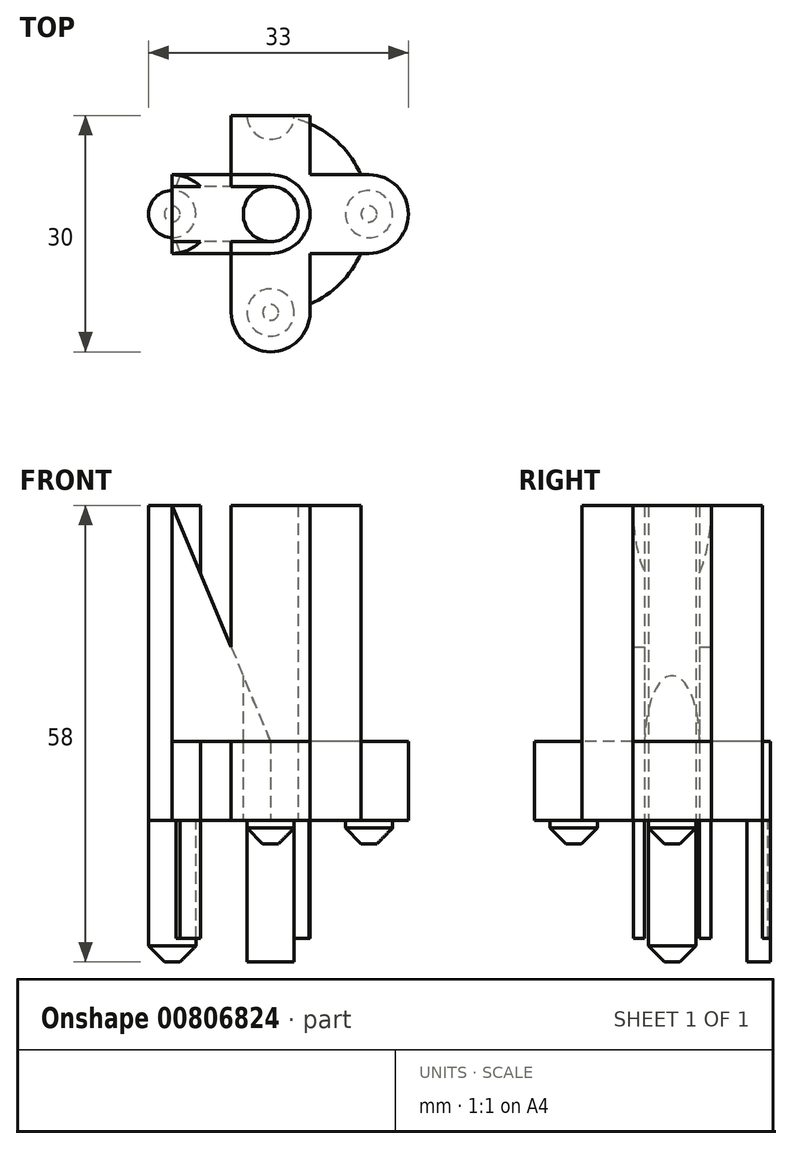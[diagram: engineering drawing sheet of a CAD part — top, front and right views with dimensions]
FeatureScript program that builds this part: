
annotation { "Feature Type Name" : "Feature", "Feature Type Description" : "" }
export const myFeature = defineFeature(function(context is Context, id is Id, definition is map)
    precondition{}
    {
        {
            var Q0;
            Q0=qCreatedBy(makeId("Top.planeOp"),FACE);
            var sketch = newSketch(context, id + "F0", { "sketchPlane" : qUnion([Q0])});
            skCircle(sketch, "E0", {"center": v(0, 0) * mm, "radius": 12.5 * mm});
            skCircle(sketch, "E1", {"center": v(0, 0) * mm, "radius": 3.5 * mm});
            skCircle(sketch, "E2", {"center": v(0, -12.5) * mm, "radius": 5 * mm});
            skCircle(sketch, "E3", {"center": v(0, 12.5) * mm, "radius": 5 * mm});
            skCircle(sketch, "E4", {"center": v(12.5, 0) * mm, "radius": 5 * mm});
            skCircle(sketch, "E5", {"center": v(-12.5, 0) * mm, "radius": 5 * mm});
            skCircle(sketch, "E6", {"center": v(-12.5, 0) * mm, "radius": 3 * mm});
            skCircle(sketch, "E7", {"center": v(0, 12.5) * mm, "radius": 3 * mm});
            skCircle(sketch, "E8", {"center": v(12.5, 0) * mm, "radius": 3 * mm});
            skCircle(sketch, "E9", {"center": v(0, -12.5) * mm, "radius": 3 * mm});
            skCircle(sketch, "E10", {"center": v(0, 0) * mm, "radius": 5 * mm});
            skLineSegment(sketch, "E11.bottom", {"start": v(0, 3.5) * mm, "end": v(-12.5, 3.5) * mm});
            skLineSegment(sketch, "E11.top", {"start": v(0, 5) * mm, "end": v(-12.5, 5) * mm});
            skLineSegment(sketch, "E11.left", {"start": v(0, 3.5) * mm, "end": v(0, 5) * mm});
            skLineSegment(sketch, "E11.right", {"start": v(-12.5, 3.5) * mm, "end": v(-12.5, 5) * mm});
            skLineSegment(sketch, "E12.bottom", {"start": v(0, -3.5) * mm, "end": v(-12.5, -3.5) * mm});
            skLineSegment(sketch, "E12.top", {"start": v(0, -5) * mm, "end": v(-12.5, -5) * mm});
            skLineSegment(sketch, "E12.left", {"start": v(0, -3.5) * mm, "end": v(0, -5) * mm});
            skLineSegment(sketch, "E12.right", {"start": v(-12.5, -3.5) * mm, "end": v(-12.5, -5) * mm});
            skLineSegment(sketch, "E13.bottom", {"start": v(5, 12.5) * mm, "end": v(-5, 12.5) * mm});
            skLineSegment(sketch, "E13.top", {"start": v(5, -12.5) * mm, "end": v(-5, -12.5) * mm});
            skLineSegment(sketch, "E13.left", {"start": v(5, 12.5) * mm, "end": v(5, -12.5) * mm});
            skLineSegment(sketch, "E13.right", {"start": v(-5, 12.5) * mm, "end": v(-5, -12.5) * mm});
            skLineSegment(sketch, "E14.bottom", {"start": v(12.5, 5) * mm, "end": v(-12.5, 5) * mm});
            skLineSegment(sketch, "E14.top", {"start": v(12.5, -5) * mm, "end": v(-12.5, -5) * mm});
            skLineSegment(sketch, "E14.left", {"start": v(12.5, 5) * mm, "end": v(12.5, -5) * mm});
            skLineSegment(sketch, "E14.right", {"start": v(-12.5, 5) * mm, "end": v(-12.5, -5) * mm});
            skSolve(sketch);
        }
        {
            var Q0;
            Q0=qCreatedBy(makeId("Front.planeOp"),FACE);
            var sketch = newSketch(context, id + "F1", { "sketchPlane" : qUnion([Q0])});
            skLineSegment(sketch, "E15", {"start": v(0, 0) * mm, "end": v(0, 10) * mm});
            skLineSegment(sketch, "E16", {"start": v(0, 10) * mm, "end": v(-12.5, 10) * mm});
            skLineSegment(sketch, "E17", {"start": v(-12.5, 10) * mm, "end": v(-12.5, 40) * mm});
            skLineSegment(sketch, "E18", {"start": v(-12.5, 40) * mm, "end": v(0, 10) * mm});
            skSolve(sketch);
        }
        {
            var Q0;
            Q0=makeQuery(id+"F1.imprint","IMPRINT",FACE,{"disambiguationData":[TD([[makeQuery(id+"F1.imprint","IMPRINT",EDGE,{"derivedFrom":sQuery(id+"F1.wireOp",EDGE,"E16")}),-1.0]])]});
            extrude(context, id + "F2", {"entities" : qUnion([Q0]), "endBound" : BoundingType.SYMMETRIC, "depth" : 10 * mm, "offsetDistance" : 25 * mm});
        }
        {
            var Q0;
            {var subQ0=sQuery(id+"F0.wireOp",EDGE,"E11.left");Q0=makeQuery(id+"F0.imprint","IMPRINT",FACE,{"disambiguationData":[TD([[makeQuery(id+"F0.imprint","IMPRINT",EDGE,{"derivedFrom":subQ0}),-1.0]])]});}
            var Q1;
            {var subQ0=sQuery(id+"F0.wireOp",EDGE,"E11.left");Q1=makeQuery(id+"F0.imprint","IMPRINT",FACE,{"disambiguationData":[TD([[makeQuery(id+"F0.imprint","IMPRINT",EDGE,{"derivedFrom":subQ0}),1.0]])]});}
            var Q2;
            {var subQ1=sQuery(id+"F0.wireOp",EDGE,"E10");var subQ3=sQuery(id+"F0.wireOp",EDGE,"E11.bottom");var subQ4=makeQuery(id+"F0.imprint","INTERSECT",VERTEX,{"derivedFrom":[subQ1,subQ3]});Q2=makeQuery(id+"F0.imprint","IMPRINT",FACE,{"disambiguationData":[TD([[makeQuery(id+"F0.imprint","IMPRINT",EDGE,{"disambiguationData":[TD([[subQ4,-1.0]])],"derivedFrom":subQ3}),-1.0]])]});}
            var Q3;
            {var subQ3=sQuery(id+"F0.wireOp",EDGE,"E14.bottom");var subQ7=sQuery(id+"F0.wireOp",EDGE,"E0");var subQ9=makeQuery(id+"F0.imprint","INTERSECT",VERTEX,{"disambiguationData":[OD(1.0)],"derivedFrom":[subQ7,subQ3]});Q3=makeQuery(id+"F0.imprint","IMPRINT",FACE,{"disambiguationData":[TD([[makeQuery(id+"F0.imprint","IMPRINT",EDGE,{"disambiguationData":[TD([[subQ9,-1.0]])],"derivedFrom":subQ7}),1.0]])]});}
            var Q4;
            {var subQ0=sQuery(id+"F0.wireOp",EDGE,"E5");var subQ1=sQuery(id+"F0.wireOp",EDGE,"E0");var subQ2=makeQuery(id+"F0.imprint","INTERSECT",VERTEX,{"disambiguationData":[OD(0.0)],"derivedFrom":[subQ1,subQ0]});Q4=makeQuery(id+"F0.imprint","IMPRINT",FACE,{"disambiguationData":[TD([[makeQuery(id+"F0.imprint","IMPRINT",EDGE,{"disambiguationData":[TD([[subQ2,-1.0]])],"derivedFrom":subQ1}),1.0]])]});}
            var Q5;
            {var subQ0=sQuery(id+"F0.wireOp",EDGE,"E5");var subQ1=sQuery(id+"F0.wireOp",EDGE,"E0");var subQ2=makeQuery(id+"F0.imprint","INTERSECT",VERTEX,{"disambiguationData":[OD(0.0)],"derivedFrom":[subQ1,subQ0]});Q5=makeQuery(id+"F0.imprint","IMPRINT",FACE,{"disambiguationData":[TD([[makeQuery(id+"F0.imprint","IMPRINT",EDGE,{"disambiguationData":[TD([[subQ2,-1.0]])],"derivedFrom":subQ1}),-1.0]])]});}
            var Q6;
            {var subQ0=sQuery(id+"F0.wireOp",EDGE,"E12.bottom");var subQ1=sQuery(id+"F0.wireOp",EDGE,"E0");var subQ2=makeQuery(id+"F0.imprint","INTERSECT",VERTEX,{"derivedFrom":[subQ1,subQ0]});Q6=makeQuery(id+"F0.imprint","IMPRINT",FACE,{"disambiguationData":[TD([[makeQuery(id+"F0.imprint","IMPRINT",EDGE,{"disambiguationData":[TD([[subQ2,-1.0]])],"derivedFrom":subQ1}),-1.0]])]});}
            var Q7;
            {var subQ0=sQuery(id+"F0.wireOp",EDGE,"E12.bottom");var subQ1=sQuery(id+"F0.wireOp",EDGE,"E0");var subQ2=makeQuery(id+"F0.imprint","INTERSECT",VERTEX,{"derivedFrom":[subQ1,subQ0]});Q7=makeQuery(id+"F0.imprint","IMPRINT",FACE,{"disambiguationData":[TD([[makeQuery(id+"F0.imprint","IMPRINT",EDGE,{"disambiguationData":[TD([[subQ2,-1.0]])],"derivedFrom":subQ1}),1.0]])]});}
            var Q8;
            {var subQ5=sQuery(id+"F0.wireOp",EDGE,"E14.top");var subQ7=sQuery(id+"F0.wireOp",EDGE,"E0");var subQ9=makeQuery(id+"F0.imprint","INTERSECT",VERTEX,{"disambiguationData":[OD(0.0)],"derivedFrom":[subQ7,subQ5]});Q8=makeQuery(id+"F0.imprint","IMPRINT",FACE,{"disambiguationData":[TD([[makeQuery(id+"F0.imprint","IMPRINT",EDGE,{"disambiguationData":[TD([[subQ9,1.0]])],"derivedFrom":subQ7}),1.0]])]});}
            var Q9;
            {var subQ1=sQuery(id+"F0.wireOp",EDGE,"E10");var subQ3=sQuery(id+"F0.wireOp",EDGE,"E12.bottom");var subQ4=makeQuery(id+"F0.imprint","INTERSECT",VERTEX,{"derivedFrom":[subQ1,subQ3]});Q9=makeQuery(id+"F0.imprint","IMPRINT",FACE,{"disambiguationData":[TD([[makeQuery(id+"F0.imprint","IMPRINT",EDGE,{"disambiguationData":[TD([[subQ4,-1.0]])],"derivedFrom":subQ3}),1.0]])]});}
            var Q10;
            {var subQ0=sQuery(id+"F0.wireOp",EDGE,"E12.left");Q10=makeQuery(id+"F0.imprint","IMPRINT",FACE,{"disambiguationData":[TD([[makeQuery(id+"F0.imprint","IMPRINT",EDGE,{"derivedFrom":subQ0}),-1.0]])]});}
            var Q11;
            {var subQ0=sQuery(id+"F0.wireOp",EDGE,"E14.top");var subQ1=sQuery(id+"F0.wireOp",EDGE,"E0");var subQ2=makeQuery(id+"F0.imprint","INTERSECT",VERTEX,{"disambiguationData":[OD(0.0)],"derivedFrom":[subQ1,subQ0]});Q11=makeQuery(id+"F0.imprint","IMPRINT",FACE,{"disambiguationData":[TD([[makeQuery(id+"F0.imprint","IMPRINT",EDGE,{"disambiguationData":[TD([[subQ2,1.0]])],"derivedFrom":subQ1}),-1.0]])]});}
            var Q12;
            {var subQ0=sQuery(id+"F0.wireOp",EDGE,"E14.bottom");var subQ1=sQuery(id+"F0.wireOp",EDGE,"E0");var subQ2=makeQuery(id+"F0.imprint","INTERSECT",VERTEX,{"disambiguationData":[OD(1.0)],"derivedFrom":[subQ1,subQ0]});Q12=makeQuery(id+"F0.imprint","IMPRINT",FACE,{"disambiguationData":[TD([[makeQuery(id+"F0.imprint","IMPRINT",EDGE,{"disambiguationData":[TD([[subQ2,-1.0]])],"derivedFrom":subQ1}),-1.0]])]});}
            var Q13;
            {var subQ0=sQuery(id+"F0.wireOp",EDGE,"E14.right");var subQ4=makeQuery(id+"F0.imprint","INTERSECT",VERTEX,{"derivedFrom":[sQuery(id+"F0.wireOp",EDGE,"E0"),subQ0]});Q13=makeQuery(id+"F0.imprint","IMPRINT",FACE,{"disambiguationData":[TD([[makeQuery(id+"F0.imprint","IMPRINT",EDGE,{"disambiguationData":[TD([[subQ4,1.0]])],"derivedFrom":subQ0}),-1.0]])]});}
            var Q14;
            {var subQ0=sQuery(id+"F0.wireOp",EDGE,"E14.right");var subQ1=sQuery(id+"F0.wireOp",EDGE,"E5");var subQ2=makeQuery(id+"F0.imprint","INTERSECT",VERTEX,{"derivedFrom":[subQ1,sQuery(id+"F0.wireOp",EDGE,"E14.bottom"),subQ0]});Q14=makeQuery(id+"F0.imprint","IMPRINT",FACE,{"disambiguationData":[TD([[makeQuery(id+"F0.imprint","IMPRINT",EDGE,{"disambiguationData":[TD([[subQ2,-1.0]])],"derivedFrom":subQ1}),1.0]])]});}
            extrude(context, id + "F3", {"entities" : qUnion([Q0, Q1, Q2, Q3, Q4, Q5, Q6, Q7, Q8, Q9, Q10, Q11, Q12, Q13, Q14]), "operationType" : NewBodyOperationType.ADD, "depth" : 40 * mm, "offsetDistance" : 25 * mm});
        }
        {
            var Q0;
            {var subQ0=sQuery(id+"F0.wireOp",EDGE,"E11.bottom");var subQ3=sQuery(id+"F0.wireOp",EDGE,"E10");var subQ4=makeQuery(id+"F0.imprint","INTERSECT",VERTEX,{"derivedFrom":[subQ3,subQ0]});Q0=makeQuery(id+"F0.imprint","IMPRINT",FACE,{"disambiguationData":[TD([[makeQuery(id+"F0.imprint","IMPRINT",EDGE,{"disambiguationData":[TD([[subQ4,-1.0]])],"derivedFrom":subQ3}),1.0]])]});}
            var Q1;
            {var subQ0=sQuery(id+"F0.wireOp",EDGE,"E11.bottom");var subQ1=sQuery(id+"F0.wireOp",EDGE,"E10");var subQ2=makeQuery(id+"F0.imprint","INTERSECT",VERTEX,{"derivedFrom":[subQ1,subQ0]});Q1=makeQuery(id+"F0.imprint","IMPRINT",FACE,{"disambiguationData":[TD([[makeQuery(id+"F0.imprint","IMPRINT",EDGE,{"disambiguationData":[TD([[subQ2,-1.0]])],"derivedFrom":subQ1}),-1.0]])]});}
            var Q2;
            {var subQ0=sQuery(id+"F0.wireOp",EDGE,"E13.right");var subQ1=sQuery(id+"F0.wireOp",EDGE,"E10");var subQ2=makeQuery(id+"F0.imprint","INTERSECT",VERTEX,{"derivedFrom":[subQ1,subQ0]});Q2=makeQuery(id+"F0.imprint","IMPRINT",FACE,{"disambiguationData":[TD([[makeQuery(id+"F0.imprint","IMPRINT",EDGE,{"disambiguationData":[TD([[subQ2,-1.0]])],"derivedFrom":subQ1}),-1.0]])]});}
            var Q3;
            {var subQ2=sQuery(id+"F0.wireOp",EDGE,"E11.bottom");var subQ5=sQuery(id+"F0.wireOp",EDGE,"E5");var subQ8=makeQuery(id+"F0.imprint","INTERSECT",VERTEX,{"derivedFrom":[subQ5,subQ2]});Q3=makeQuery(id+"F0.imprint","IMPRINT",FACE,{"disambiguationData":[TD([[makeQuery(id+"F0.imprint","IMPRINT",EDGE,{"disambiguationData":[TD([[subQ8,1.0]])],"derivedFrom":subQ5}),-1.0]])]});}
            var Q4;
            {var subQ0=sQuery(id+"F0.wireOp",EDGE,"E11.bottom");var subQ6=sQuery(id+"F0.wireOp",EDGE,"E0");var subQ10=makeQuery(id+"F0.imprint","INTERSECT",VERTEX,{"derivedFrom":[subQ6,subQ0]});Q4=makeQuery(id+"F0.imprint","IMPRINT",FACE,{"disambiguationData":[TD([[makeQuery(id+"F0.imprint","IMPRINT",EDGE,{"disambiguationData":[TD([[subQ10,-1.0]])],"derivedFrom":subQ6}),1.0]])]});}
            var Q5;
            {var subQ0=sQuery(id+"F0.wireOp",EDGE,"E6");var subQ1=sQuery(id+"F0.wireOp",EDGE,"E0");var subQ2=makeQuery(id+"F0.imprint","INTERSECT",VERTEX,{"disambiguationData":[OD(0.0)],"derivedFrom":[subQ1,subQ0]});Q5=makeQuery(id+"F0.imprint","IMPRINT",FACE,{"disambiguationData":[TD([[makeQuery(id+"F0.imprint","IMPRINT",EDGE,{"disambiguationData":[TD([[subQ2,-1.0]])],"derivedFrom":subQ1}),1.0]])]});}
            var Q6;
            {var subQ0=sQuery(id+"F0.wireOp",EDGE,"E6");var subQ1=sQuery(id+"F0.wireOp",EDGE,"E0");var subQ2=makeQuery(id+"F0.imprint","INTERSECT",VERTEX,{"disambiguationData":[OD(0.0)],"derivedFrom":[subQ1,subQ0]});Q6=makeQuery(id+"F0.imprint","IMPRINT",FACE,{"disambiguationData":[TD([[makeQuery(id+"F0.imprint","IMPRINT",EDGE,{"disambiguationData":[TD([[subQ2,-1.0]])],"derivedFrom":subQ1}),-1.0]])]});}
            var Q7;
            {var subQ0=sQuery(id+"F0.wireOp",EDGE,"E14.right");var subQ1=sQuery(id+"F0.wireOp",EDGE,"E0");var subQ2=makeQuery(id+"F0.imprint","INTERSECT",VERTEX,{"derivedFrom":[subQ1,subQ0]});Q7=makeQuery(id+"F0.imprint","IMPRINT",FACE,{"disambiguationData":[TD([[makeQuery(id+"F0.imprint","IMPRINT",EDGE,{"disambiguationData":[TD([[subQ2,-1.0]])],"derivedFrom":subQ1}),-1.0]])]});}
            var Q8;
            {var subQ0=sQuery(id+"F0.wireOp",EDGE,"E13.left");var subQ1=sQuery(id+"F0.wireOp",EDGE,"E0");var subQ2=makeQuery(id+"F0.imprint","INTERSECT",VERTEX,{"disambiguationData":[OD(0.0)],"derivedFrom":[subQ1,subQ0]});Q8=makeQuery(id+"F0.imprint","IMPRINT",FACE,{"disambiguationData":[TD([[makeQuery(id+"F0.imprint","IMPRINT",EDGE,{"disambiguationData":[TD([[subQ2,-1.0]])],"derivedFrom":subQ1}),1.0]])]});}
            var Q9;
            {var subQ0=sQuery(id+"F0.wireOp",EDGE,"E3");var subQ1=sQuery(id+"F0.wireOp",EDGE,"E0");var subQ2=makeQuery(id+"F0.imprint","INTERSECT",VERTEX,{"disambiguationData":[OD(0.0)],"derivedFrom":[subQ1,subQ0]});Q9=makeQuery(id+"F0.imprint","IMPRINT",FACE,{"disambiguationData":[TD([[makeQuery(id+"F0.imprint","IMPRINT",EDGE,{"disambiguationData":[TD([[subQ2,-1.0]])],"derivedFrom":subQ1}),1.0]])]});}
            var Q10;
            {var subQ0=sQuery(id+"F0.wireOp",EDGE,"E7");var subQ1=sQuery(id+"F0.wireOp",EDGE,"E0");var subQ2=makeQuery(id+"F0.imprint","INTERSECT",VERTEX,{"disambiguationData":[OD(0.0)],"derivedFrom":[subQ1,subQ0]});Q10=makeQuery(id+"F0.imprint","IMPRINT",FACE,{"disambiguationData":[TD([[makeQuery(id+"F0.imprint","IMPRINT",EDGE,{"disambiguationData":[TD([[subQ2,-1.0]])],"derivedFrom":subQ1}),1.0]])]});}
            var Q11;
            {var subQ0=sQuery(id+"F0.wireOp",EDGE,"E7");var subQ1=sQuery(id+"F0.wireOp",EDGE,"E0");var subQ2=makeQuery(id+"F0.imprint","INTERSECT",VERTEX,{"disambiguationData":[OD(0.0)],"derivedFrom":[subQ1,subQ0]});Q11=makeQuery(id+"F0.imprint","IMPRINT",FACE,{"disambiguationData":[TD([[makeQuery(id+"F0.imprint","IMPRINT",EDGE,{"disambiguationData":[TD([[subQ2,-1.0]])],"derivedFrom":subQ1}),-1.0]])]});}
            var Q12;
            {var subQ0=sQuery(id+"F0.wireOp",EDGE,"E3");var subQ1=sQuery(id+"F0.wireOp",EDGE,"E0");var subQ2=makeQuery(id+"F0.imprint","INTERSECT",VERTEX,{"disambiguationData":[OD(0.0)],"derivedFrom":[subQ1,subQ0]});Q12=makeQuery(id+"F0.imprint","IMPRINT",FACE,{"disambiguationData":[TD([[makeQuery(id+"F0.imprint","IMPRINT",EDGE,{"disambiguationData":[TD([[subQ2,-1.0]])],"derivedFrom":subQ1}),-1.0]])]});}
            var Q13;
            {var subQ0=sQuery(id+"F0.wireOp",EDGE,"E13.bottom");var subQ4=sQuery(id+"F0.wireOp",EDGE,"E7");var subQ5=makeQuery(id+"F0.imprint","INTERSECT",VERTEX,{"disambiguationData":[OD(0.0)],"derivedFrom":[subQ4,subQ0]});Q13=makeQuery(id+"F0.imprint","IMPRINT",FACE,{"disambiguationData":[TD([[makeQuery(id+"F0.imprint","IMPRINT",EDGE,{"disambiguationData":[TD([[subQ5,1.0]])],"derivedFrom":subQ4}),-1.0]])]});}
            var Q14;
            {var subQ0=sQuery(id+"F0.wireOp",EDGE,"E13.bottom");var subQ1=sQuery(id+"F0.wireOp",EDGE,"E7");var subQ2=makeQuery(id+"F0.imprint","INTERSECT",VERTEX,{"disambiguationData":[OD(0.0)],"derivedFrom":[subQ1,subQ0]});Q14=makeQuery(id+"F0.imprint","IMPRINT",FACE,{"disambiguationData":[TD([[makeQuery(id+"F0.imprint","IMPRINT",EDGE,{"disambiguationData":[TD([[subQ2,1.0]])],"derivedFrom":subQ1}),1.0]])]});}
            var Q15;
            {var subQ0=sQuery(id+"F0.wireOp",EDGE,"E13.bottom");var subQ1=sQuery(id+"F0.wireOp",EDGE,"E0");var subQ2=makeQuery(id+"F0.imprint","INTERSECT",VERTEX,{"derivedFrom":[subQ1,subQ0]});Q15=makeQuery(id+"F0.imprint","IMPRINT",FACE,{"disambiguationData":[TD([[makeQuery(id+"F0.imprint","IMPRINT",EDGE,{"disambiguationData":[TD([[subQ2,-1.0]])],"derivedFrom":subQ1}),-1.0]])]});}
            var Q16;
            {var subQ0=sQuery(id+"F0.wireOp",EDGE,"E7");var subQ1=sQuery(id+"F0.wireOp",EDGE,"E0");var subQ2=makeQuery(id+"F0.imprint","INTERSECT",VERTEX,{"disambiguationData":[OD(1.0)],"derivedFrom":[subQ1,subQ0]});Q16=makeQuery(id+"F0.imprint","IMPRINT",FACE,{"disambiguationData":[TD([[makeQuery(id+"F0.imprint","IMPRINT",EDGE,{"disambiguationData":[TD([[subQ2,-1.0]])],"derivedFrom":subQ1}),-1.0]])]});}
            var Q17;
            {var subQ0=sQuery(id+"F0.wireOp",EDGE,"E8");var subQ1=sQuery(id+"F0.wireOp",EDGE,"E0");var subQ2=makeQuery(id+"F0.imprint","INTERSECT",VERTEX,{"disambiguationData":[OD(0.0)],"derivedFrom":[subQ1,subQ0]});Q17=makeQuery(id+"F0.imprint","IMPRINT",FACE,{"disambiguationData":[TD([[makeQuery(id+"F0.imprint","IMPRINT",EDGE,{"disambiguationData":[TD([[subQ2,-1.0]])],"derivedFrom":subQ1}),1.0]])]});}
            var Q18;
            {var subQ0=sQuery(id+"F0.wireOp",EDGE,"E8");var subQ1=sQuery(id+"F0.wireOp",EDGE,"E0");var subQ2=makeQuery(id+"F0.imprint","INTERSECT",VERTEX,{"disambiguationData":[OD(0.0)],"derivedFrom":[subQ1,subQ0]});Q18=makeQuery(id+"F0.imprint","IMPRINT",FACE,{"disambiguationData":[TD([[makeQuery(id+"F0.imprint","IMPRINT",EDGE,{"disambiguationData":[TD([[subQ2,-1.0]])],"derivedFrom":subQ1}),-1.0]])]});}
            var Q19;
            {var subQ0=sQuery(id+"F0.wireOp",EDGE,"E14.left");var subQ4=sQuery(id+"F0.wireOp",EDGE,"E8");var subQ5=makeQuery(id+"F0.imprint","INTERSECT",VERTEX,{"disambiguationData":[OD(0.0)],"derivedFrom":[subQ4,subQ0]});Q19=makeQuery(id+"F0.imprint","IMPRINT",FACE,{"disambiguationData":[TD([[makeQuery(id+"F0.imprint","IMPRINT",EDGE,{"disambiguationData":[TD([[subQ5,1.0]])],"derivedFrom":subQ4}),-1.0]])]});}
            var Q20;
            {var subQ0=sQuery(id+"F0.wireOp",EDGE,"E14.left");var subQ1=sQuery(id+"F0.wireOp",EDGE,"E8");var subQ2=makeQuery(id+"F0.imprint","INTERSECT",VERTEX,{"disambiguationData":[OD(0.0)],"derivedFrom":[subQ1,subQ0]});Q20=makeQuery(id+"F0.imprint","IMPRINT",FACE,{"disambiguationData":[TD([[makeQuery(id+"F0.imprint","IMPRINT",EDGE,{"disambiguationData":[TD([[subQ2,1.0]])],"derivedFrom":subQ1}),1.0]])]});}
            var Q21;
            {var subQ0=sQuery(id+"F0.wireOp",EDGE,"E8");var subQ1=sQuery(id+"F0.wireOp",EDGE,"E0");var subQ2=makeQuery(id+"F0.imprint","INTERSECT",VERTEX,{"disambiguationData":[OD(0.0)],"derivedFrom":[subQ1,subQ0]});Q21=makeQuery(id+"F0.imprint","IMPRINT",FACE,{"disambiguationData":[TD([[makeQuery(id+"F0.imprint","IMPRINT",EDGE,{"disambiguationData":[TD([[subQ2,1.0]])],"derivedFrom":subQ1}),1.0]])]});}
            var Q22;
            {var subQ0=sQuery(id+"F0.wireOp",EDGE,"E8");var subQ1=sQuery(id+"F0.wireOp",EDGE,"E0");var subQ2=makeQuery(id+"F0.imprint","INTERSECT",VERTEX,{"disambiguationData":[OD(0.0)],"derivedFrom":[subQ1,subQ0]});Q22=makeQuery(id+"F0.imprint","IMPRINT",FACE,{"disambiguationData":[TD([[makeQuery(id+"F0.imprint","IMPRINT",EDGE,{"disambiguationData":[TD([[subQ2,1.0]])],"derivedFrom":subQ1}),-1.0]])]});}
            var Q23;
            {var subQ0=sQuery(id+"F0.wireOp",EDGE,"E14.left");var subQ1=sQuery(id+"F0.wireOp",EDGE,"E0");var subQ2=makeQuery(id+"F0.imprint","INTERSECT",VERTEX,{"derivedFrom":[subQ1,subQ0]});Q23=makeQuery(id+"F0.imprint","IMPRINT",FACE,{"disambiguationData":[TD([[makeQuery(id+"F0.imprint","IMPRINT",EDGE,{"disambiguationData":[TD([[subQ2,1.0]])],"derivedFrom":subQ1}),-1.0]])]});}
            var Q24;
            {var subQ0=sQuery(id+"F0.wireOp",EDGE,"E4");var subQ1=sQuery(id+"F0.wireOp",EDGE,"E0");var subQ2=makeQuery(id+"F0.imprint","INTERSECT",VERTEX,{"disambiguationData":[OD(1.0)],"derivedFrom":[subQ1,subQ0]});Q24=makeQuery(id+"F0.imprint","IMPRINT",FACE,{"disambiguationData":[TD([[makeQuery(id+"F0.imprint","IMPRINT",EDGE,{"disambiguationData":[TD([[subQ2,-1.0]])],"derivedFrom":subQ1}),-1.0]])]});}
            var Q25;
            {var subQ2=sQuery(id+"F0.wireOp",EDGE,"E14.bottom");var subQ5=sQuery(id+"F0.wireOp",EDGE,"E0");var subQ8=makeQuery(id+"F0.imprint","INTERSECT",VERTEX,{"disambiguationData":[OD(0.0)],"derivedFrom":[subQ5,subQ2]});Q25=makeQuery(id+"F0.imprint","IMPRINT",FACE,{"disambiguationData":[TD([[makeQuery(id+"F0.imprint","IMPRINT",EDGE,{"disambiguationData":[TD([[subQ8,1.0]])],"derivedFrom":subQ5}),1.0]])]});}
            var Q26;
            {var subQ0=sQuery(id+"F0.wireOp",EDGE,"E13.left");var subQ1=sQuery(id+"F0.wireOp",EDGE,"E0");var subQ2=makeQuery(id+"F0.imprint","INTERSECT",VERTEX,{"disambiguationData":[OD(0.0)],"derivedFrom":[subQ1,subQ0]});Q26=makeQuery(id+"F0.imprint","IMPRINT",FACE,{"disambiguationData":[TD([[makeQuery(id+"F0.imprint","IMPRINT",EDGE,{"disambiguationData":[TD([[subQ2,-1.0]])],"derivedFrom":subQ1}),-1.0]])]});}
            var Q27;
            {var subQ0=sQuery(id+"F0.wireOp",EDGE,"E13.right");var subQ1=sQuery(id+"F0.wireOp",EDGE,"E0");var subQ2=makeQuery(id+"F0.imprint","INTERSECT",VERTEX,{"disambiguationData":[OD(0.0)],"derivedFrom":[subQ1,subQ0]});Q27=makeQuery(id+"F0.imprint","IMPRINT",FACE,{"disambiguationData":[TD([[makeQuery(id+"F0.imprint","IMPRINT",EDGE,{"disambiguationData":[TD([[subQ2,1.0]])],"derivedFrom":subQ1}),-1.0]])]});}
            var Q28;
            {var subQ0=sQuery(id+"F0.wireOp",EDGE,"E14.bottom");var subQ1=sQuery(id+"F0.wireOp",EDGE,"E0");var subQ2=makeQuery(id+"F0.imprint","INTERSECT",VERTEX,{"disambiguationData":[OD(0.0)],"derivedFrom":[subQ1,subQ0]});Q28=makeQuery(id+"F0.imprint","IMPRINT",FACE,{"disambiguationData":[TD([[makeQuery(id+"F0.imprint","IMPRINT",EDGE,{"disambiguationData":[TD([[subQ2,1.0]])],"derivedFrom":subQ1}),-1.0]])]});}
            var Q29;
            {var subQ0=sQuery(id+"F0.wireOp",EDGE,"E14.top");var subQ1=sQuery(id+"F0.wireOp",EDGE,"E0");var subQ2=makeQuery(id+"F0.imprint","INTERSECT",VERTEX,{"disambiguationData":[OD(1.0)],"derivedFrom":[subQ1,subQ0]});Q29=makeQuery(id+"F0.imprint","IMPRINT",FACE,{"disambiguationData":[TD([[makeQuery(id+"F0.imprint","IMPRINT",EDGE,{"disambiguationData":[TD([[subQ2,-1.0]])],"derivedFrom":subQ1}),-1.0]])]});}
            var Q30;
            {var subQ0=sQuery(id+"F0.wireOp",EDGE,"E13.top");var subQ4=sQuery(id+"F0.wireOp",EDGE,"E9");var subQ5=makeQuery(id+"F0.imprint","INTERSECT",VERTEX,{"disambiguationData":[OD(0.0)],"derivedFrom":[subQ4,subQ0]});Q30=makeQuery(id+"F0.imprint","IMPRINT",FACE,{"disambiguationData":[TD([[makeQuery(id+"F0.imprint","IMPRINT",EDGE,{"disambiguationData":[TD([[subQ5,1.0]])],"derivedFrom":subQ4}),-1.0]])]});}
            var Q31;
            {var subQ0=sQuery(id+"F0.wireOp",EDGE,"E13.top");var subQ1=sQuery(id+"F0.wireOp",EDGE,"E0");var subQ2=makeQuery(id+"F0.imprint","INTERSECT",VERTEX,{"derivedFrom":[subQ1,subQ0]});Q31=makeQuery(id+"F0.imprint","IMPRINT",FACE,{"disambiguationData":[TD([[makeQuery(id+"F0.imprint","IMPRINT",EDGE,{"disambiguationData":[TD([[subQ2,-1.0]])],"derivedFrom":subQ1}),-1.0]])]});}
            var Q32;
            {var subQ0=sQuery(id+"F0.wireOp",EDGE,"E9");var subQ1=sQuery(id+"F0.wireOp",EDGE,"E0");var subQ2=makeQuery(id+"F0.imprint","INTERSECT",VERTEX,{"disambiguationData":[OD(1.0)],"derivedFrom":[subQ1,subQ0]});Q32=makeQuery(id+"F0.imprint","IMPRINT",FACE,{"disambiguationData":[TD([[makeQuery(id+"F0.imprint","IMPRINT",EDGE,{"disambiguationData":[TD([[subQ2,-1.0]])],"derivedFrom":subQ1}),-1.0]])]});}
            var Q33;
            {var subQ0=sQuery(id+"F0.wireOp",EDGE,"E13.top");var subQ1=sQuery(id+"F0.wireOp",EDGE,"E9");var subQ2=makeQuery(id+"F0.imprint","INTERSECT",VERTEX,{"disambiguationData":[OD(0.0)],"derivedFrom":[subQ1,subQ0]});Q33=makeQuery(id+"F0.imprint","IMPRINT",FACE,{"disambiguationData":[TD([[makeQuery(id+"F0.imprint","IMPRINT",EDGE,{"disambiguationData":[TD([[subQ2,1.0]])],"derivedFrom":subQ1}),1.0]])]});}
            var Q34;
            {var subQ0=sQuery(id+"F0.wireOp",EDGE,"E9");var subQ1=sQuery(id+"F0.wireOp",EDGE,"E0");var subQ2=makeQuery(id+"F0.imprint","INTERSECT",VERTEX,{"disambiguationData":[OD(0.0)],"derivedFrom":[subQ1,subQ0]});Q34=makeQuery(id+"F0.imprint","IMPRINT",FACE,{"disambiguationData":[TD([[makeQuery(id+"F0.imprint","IMPRINT",EDGE,{"disambiguationData":[TD([[subQ2,-1.0]])],"derivedFrom":subQ1}),1.0]])]});}
            var Q35;
            {var subQ0=sQuery(id+"F0.wireOp",EDGE,"E2");var subQ1=sQuery(id+"F0.wireOp",EDGE,"E0");var subQ2=makeQuery(id+"F0.imprint","INTERSECT",VERTEX,{"disambiguationData":[OD(0.0)],"derivedFrom":[subQ1,subQ0]});Q35=makeQuery(id+"F0.imprint","IMPRINT",FACE,{"disambiguationData":[TD([[makeQuery(id+"F0.imprint","IMPRINT",EDGE,{"disambiguationData":[TD([[subQ2,-1.0]])],"derivedFrom":subQ1}),1.0]])]});}
            var Q36;
            {var subQ0=sQuery(id+"F0.wireOp",EDGE,"E2");var subQ1=sQuery(id+"F0.wireOp",EDGE,"E0");var subQ2=makeQuery(id+"F0.imprint","INTERSECT",VERTEX,{"disambiguationData":[OD(0.0)],"derivedFrom":[subQ1,subQ0]});Q36=makeQuery(id+"F0.imprint","IMPRINT",FACE,{"disambiguationData":[TD([[makeQuery(id+"F0.imprint","IMPRINT",EDGE,{"disambiguationData":[TD([[subQ2,-1.0]])],"derivedFrom":subQ1}),-1.0]])]});}
            var Q37;
            {var subQ0=sQuery(id+"F0.wireOp",EDGE,"E9");var subQ1=sQuery(id+"F0.wireOp",EDGE,"E0");var subQ2=makeQuery(id+"F0.imprint","INTERSECT",VERTEX,{"disambiguationData":[OD(0.0)],"derivedFrom":[subQ1,subQ0]});Q37=makeQuery(id+"F0.imprint","IMPRINT",FACE,{"disambiguationData":[TD([[makeQuery(id+"F0.imprint","IMPRINT",EDGE,{"disambiguationData":[TD([[subQ2,-1.0]])],"derivedFrom":subQ1}),-1.0]])]});}
            var Q38;
            {var subQ1=sQuery(id+"F0.wireOp",EDGE,"E0");var subQ8=sQuery(id+"F0.wireOp",EDGE,"E13.right");var subQ9=makeQuery(id+"F0.imprint","INTERSECT",VERTEX,{"disambiguationData":[OD(1.0)],"derivedFrom":[subQ1,subQ8]});Q38=makeQuery(id+"F0.imprint","IMPRINT",FACE,{"disambiguationData":[TD([[makeQuery(id+"F0.imprint","IMPRINT",EDGE,{"disambiguationData":[TD([[subQ9,-1.0]])],"derivedFrom":subQ1}),1.0]])]});}
            var Q39;
            {var subQ0=sQuery(id+"F0.wireOp",EDGE,"E13.left");var subQ1=sQuery(id+"F0.wireOp",EDGE,"E0");var subQ2=makeQuery(id+"F0.imprint","INTERSECT",VERTEX,{"disambiguationData":[OD(1.0)],"derivedFrom":[subQ1,subQ0]});Q39=makeQuery(id+"F0.imprint","IMPRINT",FACE,{"disambiguationData":[TD([[makeQuery(id+"F0.imprint","IMPRINT",EDGE,{"disambiguationData":[TD([[subQ2,1.0]])],"derivedFrom":subQ1}),-1.0]])]});}
            var Q40;
            {var subQ0=sQuery(id+"F0.wireOp",EDGE,"E13.right");var subQ1=sQuery(id+"F0.wireOp",EDGE,"E0");var subQ2=makeQuery(id+"F0.imprint","INTERSECT",VERTEX,{"disambiguationData":[OD(1.0)],"derivedFrom":[subQ1,subQ0]});Q40=makeQuery(id+"F0.imprint","IMPRINT",FACE,{"disambiguationData":[TD([[makeQuery(id+"F0.imprint","IMPRINT",EDGE,{"disambiguationData":[TD([[subQ2,-1.0]])],"derivedFrom":subQ1}),-1.0]])]});}
            var Q41;
            {var subQ1=sQuery(id+"F0.wireOp",EDGE,"E10");var subQ3=sQuery(id+"F0.wireOp",EDGE,"E13.left");var subQ4=makeQuery(id+"F0.imprint","INTERSECT",VERTEX,{"derivedFrom":[subQ1,subQ3]});Q41=makeQuery(id+"F0.imprint","IMPRINT",FACE,{"disambiguationData":[TD([[makeQuery(id+"F0.imprint","IMPRINT",EDGE,{"disambiguationData":[TD([[subQ4,1.0]])],"derivedFrom":subQ3}),-1.0]])]});}
            var Q42;
            {var subQ1=sQuery(id+"F0.wireOp",EDGE,"E10");var subQ3=sQuery(id+"F0.wireOp",EDGE,"E13.left");var subQ4=makeQuery(id+"F0.imprint","INTERSECT",VERTEX,{"derivedFrom":[subQ1,subQ3]});Q42=makeQuery(id+"F0.imprint","IMPRINT",FACE,{"disambiguationData":[TD([[makeQuery(id+"F0.imprint","IMPRINT",EDGE,{"disambiguationData":[TD([[subQ4,-1.0]])],"derivedFrom":subQ3}),-1.0]])]});}
            var Q43;
            {var subQ0=sQuery(id+"F0.wireOp",EDGE,"E6");var subQ1=sQuery(id+"F0.wireOp",EDGE,"E0");var subQ2=makeQuery(id+"F0.imprint","INTERSECT",VERTEX,{"disambiguationData":[OD(1.0)],"derivedFrom":[subQ1,subQ0]});Q43=makeQuery(id+"F0.imprint","IMPRINT",FACE,{"disambiguationData":[TD([[makeQuery(id+"F0.imprint","IMPRINT",EDGE,{"disambiguationData":[TD([[subQ2,-1.0]])],"derivedFrom":subQ1}),-1.0]])]});}
            var Q44;
            {var subQ0=sQuery(id+"F0.wireOp",EDGE,"E11.bottom");var subQ1=sQuery(id+"F0.wireOp",EDGE,"E0");var subQ2=makeQuery(id+"F0.imprint","INTERSECT",VERTEX,{"derivedFrom":[subQ1,subQ0]});Q44=makeQuery(id+"F0.imprint","IMPRINT",FACE,{"disambiguationData":[TD([[makeQuery(id+"F0.imprint","IMPRINT",EDGE,{"disambiguationData":[TD([[subQ2,-1.0]])],"derivedFrom":subQ1}),-1.0]])]});}
            extrude(context, id + "F4", {"entities" : qUnion([Q0, Q1, Q2, Q3, Q4, Q5, Q6, Q7, Q8, Q9, Q10, Q11, Q12, Q13, Q14, Q15, Q16, Q17, Q18, Q19, Q20, Q21, Q22, Q23, Q24, Q25, Q26, Q27, Q28, Q29, Q30, Q31, Q32, Q33, Q34, Q35, Q36, Q37, Q38, Q39, Q40, Q41, Q42, Q43, Q44]), "depth" : 10 * mm, "offsetDistance" : 25 * mm});
        }
        {
            var Q0;
            {var subQ0=sQuery(id+"F0.wireOp",EDGE,"E1");var subQ1=makeQuery(id+"F0.imprint","INTERSECT",VERTEX,{"derivedFrom":[subQ0,sQuery(id+"F0.wireOp",EDGE,"E11.bottom"),sQuery(id+"F0.wireOp",EDGE,"E11.left")]});Q0=makeQuery(id+"F0.imprint","IMPRINT",FACE,{"disambiguationData":[TD([[makeQuery(id+"F0.imprint","IMPRINT",EDGE,{"disambiguationData":[TD([[subQ1,-1.0]])],"derivedFrom":subQ0}),1.0]])]});}
            extrude(context, id + "F5", {"entities" : qUnion([Q0]), "operationType" : NewBodyOperationType.REMOVE, "oppositeDirection" : true, "depth" : -40 * mm, "offsetDistance" : 25 * mm});
        }
        {
            var Q0;
            {var subQ0=sQuery(id+"F0.wireOp",EDGE,"E14.right");var subQ1=sQuery(id+"F0.wireOp",EDGE,"E5");var subQ2=makeQuery(id+"F0.imprint","INTERSECT",VERTEX,{"derivedFrom":[subQ1,sQuery(id+"F0.wireOp",EDGE,"E14.bottom"),subQ0]});Q0=makeQuery(id+"F0.imprint","IMPRINT",FACE,{"disambiguationData":[TD([[makeQuery(id+"F0.imprint","IMPRINT",EDGE,{"disambiguationData":[TD([[subQ2,-1.0]])],"derivedFrom":subQ1}),1.0]])]});}
            var Q1;
            {var subQ0=sQuery(id+"F0.wireOp",EDGE,"E13.bottom");var subQ4=sQuery(id+"F0.wireOp",EDGE,"E7");var subQ5=makeQuery(id+"F0.imprint","INTERSECT",VERTEX,{"disambiguationData":[OD(0.0)],"derivedFrom":[subQ4,subQ0]});Q1=makeQuery(id+"F0.imprint","IMPRINT",FACE,{"disambiguationData":[TD([[makeQuery(id+"F0.imprint","IMPRINT",EDGE,{"disambiguationData":[TD([[subQ5,1.0]])],"derivedFrom":subQ4}),-1.0]])]});}
            extrude(context, id + "F6", {"entities" : qUnion([Q0, Q1]), "oppositeDirection" : true, "depth" : 15 * mm, "offsetDistance" : 25 * mm});
        }
        {
            var Q0;
            {var subQ0=sQuery(id+"F0.wireOp",EDGE,"E14.right");var subQ4=makeQuery(id+"F0.imprint","INTERSECT",VERTEX,{"derivedFrom":[sQuery(id+"F0.wireOp",EDGE,"E0"),subQ0]});Q0=makeQuery(id+"F0.imprint","IMPRINT",FACE,{"disambiguationData":[TD([[makeQuery(id+"F0.imprint","IMPRINT",EDGE,{"disambiguationData":[TD([[subQ4,1.0]])],"derivedFrom":subQ0}),-1.0]])]});}
            var Q1;
            {var subQ0=sQuery(id+"F0.wireOp",EDGE,"E14.right");var subQ1=sQuery(id+"F0.wireOp",EDGE,"E0");var subQ2=makeQuery(id+"F0.imprint","INTERSECT",VERTEX,{"derivedFrom":[subQ1,subQ0]});Q1=makeQuery(id+"F0.imprint","IMPRINT",FACE,{"disambiguationData":[TD([[makeQuery(id+"F0.imprint","IMPRINT",EDGE,{"disambiguationData":[TD([[subQ2,-1.0]])],"derivedFrom":subQ1}),-1.0]])]});}
            var Q2;
            {var subQ0=sQuery(id+"F0.wireOp",EDGE,"E6");var subQ1=sQuery(id+"F0.wireOp",EDGE,"E0");var subQ2=makeQuery(id+"F0.imprint","INTERSECT",VERTEX,{"disambiguationData":[OD(0.0)],"derivedFrom":[subQ1,subQ0]});Q2=makeQuery(id+"F0.imprint","IMPRINT",FACE,{"disambiguationData":[TD([[makeQuery(id+"F0.imprint","IMPRINT",EDGE,{"disambiguationData":[TD([[subQ2,-1.0]])],"derivedFrom":subQ1}),1.0]])]});}
            var Q3;
            {var subQ0=sQuery(id+"F0.wireOp",EDGE,"E6");var subQ1=sQuery(id+"F0.wireOp",EDGE,"E0");var subQ2=makeQuery(id+"F0.imprint","INTERSECT",VERTEX,{"disambiguationData":[OD(0.0)],"derivedFrom":[subQ1,subQ0]});Q3=makeQuery(id+"F0.imprint","IMPRINT",FACE,{"disambiguationData":[TD([[makeQuery(id+"F0.imprint","IMPRINT",EDGE,{"disambiguationData":[TD([[subQ2,-1.0]])],"derivedFrom":subQ1}),-1.0]])]});}
            var Q4;
            {var subQ0=sQuery(id+"F0.wireOp",EDGE,"E7");var subQ1=sQuery(id+"F0.wireOp",EDGE,"E0");var subQ2=makeQuery(id+"F0.imprint","INTERSECT",VERTEX,{"disambiguationData":[OD(0.0)],"derivedFrom":[subQ1,subQ0]});Q4=makeQuery(id+"F0.imprint","IMPRINT",FACE,{"disambiguationData":[TD([[makeQuery(id+"F0.imprint","IMPRINT",EDGE,{"disambiguationData":[TD([[subQ2,-1.0]])],"derivedFrom":subQ1}),1.0]])]});}
            var Q5;
            {var subQ0=sQuery(id+"F0.wireOp",EDGE,"E7");var subQ1=sQuery(id+"F0.wireOp",EDGE,"E0");var subQ2=makeQuery(id+"F0.imprint","INTERSECT",VERTEX,{"disambiguationData":[OD(0.0)],"derivedFrom":[subQ1,subQ0]});Q5=makeQuery(id+"F0.imprint","IMPRINT",FACE,{"disambiguationData":[TD([[makeQuery(id+"F0.imprint","IMPRINT",EDGE,{"disambiguationData":[TD([[subQ2,-1.0]])],"derivedFrom":subQ1}),-1.0]])]});}
            var Q6;
            {var subQ0=sQuery(id+"F0.wireOp",EDGE,"E13.bottom");var subQ1=sQuery(id+"F0.wireOp",EDGE,"E0");var subQ2=makeQuery(id+"F0.imprint","INTERSECT",VERTEX,{"derivedFrom":[subQ1,subQ0]});Q6=makeQuery(id+"F0.imprint","IMPRINT",FACE,{"disambiguationData":[TD([[makeQuery(id+"F0.imprint","IMPRINT",EDGE,{"disambiguationData":[TD([[subQ2,-1.0]])],"derivedFrom":subQ1}),-1.0]])]});}
            var Q7;
            {var subQ0=sQuery(id+"F0.wireOp",EDGE,"E13.bottom");var subQ1=sQuery(id+"F0.wireOp",EDGE,"E7");var subQ2=makeQuery(id+"F0.imprint","INTERSECT",VERTEX,{"disambiguationData":[OD(0.0)],"derivedFrom":[subQ1,subQ0]});Q7=makeQuery(id+"F0.imprint","IMPRINT",FACE,{"disambiguationData":[TD([[makeQuery(id+"F0.imprint","IMPRINT",EDGE,{"disambiguationData":[TD([[subQ2,1.0]])],"derivedFrom":subQ1}),1.0]])]});}
            extrude(context, id + "F7", {"entities" : qUnion([Q0, Q1, Q2, Q3, Q4, Q5, Q6, Q7]), "oppositeDirection" : true, "depth" : 18 * mm, "offsetDistance" : 25 * mm});
        }
        {
            var Q0;
            Q0=makeQuery(id+"F7.opExtrude","CAP_FACE",FACE,{"disambiguationData":[OSD([sQuery(id+"F0.wireOp",EDGE,"E6")])],"isStart":false});
            var Q1;
            Q1=makeQuery(id+"F7.opExtrude","CAP_FACE",FACE,{"disambiguationData":[OSD([sQuery(id+"F0.wireOp",EDGE,"E7")])],"isStart":false});
            chamfer(context, id + "F8", {"entities" : qUnion([Q0, Q1]), "width" : 2 * mm, "tangentPropagation" : true});
        }
        {
            var Q0;
            {var subQ0=sQuery(id+"F0.wireOp",EDGE,"E14.left");var subQ1=sQuery(id+"F0.wireOp",EDGE,"E0");var subQ2=makeQuery(id+"F0.imprint","INTERSECT",VERTEX,{"derivedFrom":[subQ1,subQ0]});Q0=makeQuery(id+"F0.imprint","IMPRINT",FACE,{"disambiguationData":[TD([[makeQuery(id+"F0.imprint","IMPRINT",EDGE,{"disambiguationData":[TD([[subQ2,1.0]])],"derivedFrom":subQ1}),-1.0]])]});}
            var Q1;
            {var subQ0=sQuery(id+"F0.wireOp",EDGE,"E8");var subQ1=sQuery(id+"F0.wireOp",EDGE,"E0");var subQ2=makeQuery(id+"F0.imprint","INTERSECT",VERTEX,{"disambiguationData":[OD(0.0)],"derivedFrom":[subQ1,subQ0]});Q1=makeQuery(id+"F0.imprint","IMPRINT",FACE,{"disambiguationData":[TD([[makeQuery(id+"F0.imprint","IMPRINT",EDGE,{"disambiguationData":[TD([[subQ2,1.0]])],"derivedFrom":subQ1}),1.0]])]});}
            var Q2;
            {var subQ0=sQuery(id+"F0.wireOp",EDGE,"E8");var subQ1=sQuery(id+"F0.wireOp",EDGE,"E0");var subQ2=makeQuery(id+"F0.imprint","INTERSECT",VERTEX,{"disambiguationData":[OD(0.0)],"derivedFrom":[subQ1,subQ0]});Q2=makeQuery(id+"F0.imprint","IMPRINT",FACE,{"disambiguationData":[TD([[makeQuery(id+"F0.imprint","IMPRINT",EDGE,{"disambiguationData":[TD([[subQ2,1.0]])],"derivedFrom":subQ1}),-1.0]])]});}
            var Q3;
            {var subQ0=sQuery(id+"F0.wireOp",EDGE,"E14.left");var subQ1=sQuery(id+"F0.wireOp",EDGE,"E8");var subQ2=makeQuery(id+"F0.imprint","INTERSECT",VERTEX,{"disambiguationData":[OD(0.0)],"derivedFrom":[subQ1,subQ0]});Q3=makeQuery(id+"F0.imprint","IMPRINT",FACE,{"disambiguationData":[TD([[makeQuery(id+"F0.imprint","IMPRINT",EDGE,{"disambiguationData":[TD([[subQ2,1.0]])],"derivedFrom":subQ1}),1.0]])]});}
            var Q4;
            {var subQ0=sQuery(id+"F0.wireOp",EDGE,"E13.top");var subQ1=sQuery(id+"F0.wireOp",EDGE,"E9");var subQ2=makeQuery(id+"F0.imprint","INTERSECT",VERTEX,{"disambiguationData":[OD(0.0)],"derivedFrom":[subQ1,subQ0]});Q4=makeQuery(id+"F0.imprint","IMPRINT",FACE,{"disambiguationData":[TD([[makeQuery(id+"F0.imprint","IMPRINT",EDGE,{"disambiguationData":[TD([[subQ2,1.0]])],"derivedFrom":subQ1}),1.0]])]});}
            var Q5;
            {var subQ0=sQuery(id+"F0.wireOp",EDGE,"E9");var subQ1=sQuery(id+"F0.wireOp",EDGE,"E0");var subQ2=makeQuery(id+"F0.imprint","INTERSECT",VERTEX,{"disambiguationData":[OD(0.0)],"derivedFrom":[subQ1,subQ0]});Q5=makeQuery(id+"F0.imprint","IMPRINT",FACE,{"disambiguationData":[TD([[makeQuery(id+"F0.imprint","IMPRINT",EDGE,{"disambiguationData":[TD([[subQ2,-1.0]])],"derivedFrom":subQ1}),1.0]])]});}
            var Q6;
            {var subQ0=sQuery(id+"F0.wireOp",EDGE,"E13.top");var subQ1=sQuery(id+"F0.wireOp",EDGE,"E0");var subQ2=makeQuery(id+"F0.imprint","INTERSECT",VERTEX,{"derivedFrom":[subQ1,subQ0]});Q6=makeQuery(id+"F0.imprint","IMPRINT",FACE,{"disambiguationData":[TD([[makeQuery(id+"F0.imprint","IMPRINT",EDGE,{"disambiguationData":[TD([[subQ2,-1.0]])],"derivedFrom":subQ1}),-1.0]])]});}
            var Q7;
            {var subQ0=sQuery(id+"F0.wireOp",EDGE,"E9");var subQ1=sQuery(id+"F0.wireOp",EDGE,"E0");var subQ2=makeQuery(id+"F0.imprint","INTERSECT",VERTEX,{"disambiguationData":[OD(0.0)],"derivedFrom":[subQ1,subQ0]});Q7=makeQuery(id+"F0.imprint","IMPRINT",FACE,{"disambiguationData":[TD([[makeQuery(id+"F0.imprint","IMPRINT",EDGE,{"disambiguationData":[TD([[subQ2,-1.0]])],"derivedFrom":subQ1}),-1.0]])]});}
            extrude(context, id + "F9", {"entities" : qUnion([Q0, Q1, Q2, Q3, Q4, Q5, Q6, Q7]), "operationType" : NewBodyOperationType.ADD, "oppositeDirection" : true, "depth" : 3 * mm, "offsetDistance" : 25 * mm});
        }
        {
            var Q0;
            Q0=makeQuery(id+"F9.opExtrude","CAP_FACE",FACE,{"disambiguationData":[OSD([sQuery(id+"F0.wireOp",EDGE,"E9")])],"isStart":false});
            var Q1;
            Q1=makeQuery(id+"F9.opExtrude","CAP_FACE",FACE,{"disambiguationData":[OSD([sQuery(id+"F0.wireOp",EDGE,"E8")])],"isStart":false});
            chamfer(context, id + "F10", {"entities" : qUnion([Q0, Q1]), "width" : 2 * mm, "tangentPropagation" : true});
        }
    });
